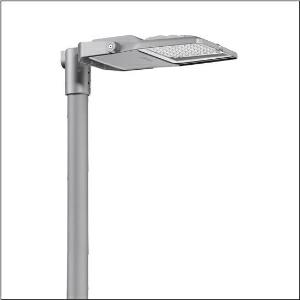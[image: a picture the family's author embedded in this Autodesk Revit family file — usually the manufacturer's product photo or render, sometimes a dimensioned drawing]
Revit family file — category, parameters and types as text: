
# Revit family: floodlight_fl_21_iq_mini___pl52_5xa7772c2d3a_4b1a
name_source: partatom
category: Lighting Fixtures
units: mm (PartAtom-declared; Revit-internal decimal feet)

## family parameters
Cut with Voids When Loaded = No
Host = Face
Light Source = No
Part Type = Normal
Room Calculation Point = No
Round Connector Dimension = Use Diameter
Shared = No

## types (1)
- --- (1 x LED, 12210 lm, 87.2 W, 3000K)
    Apparent Load = 87 VA
    CIE Flux Codes = 26 60 98 100 100
    Color Rendering = 70
    Color Temperature = 3000K
    Default Elevation = 1800 mm
    Description = Floodlight FL 21 iQ mini, floodlight, primary light control with lens, of PMMA, primary optical cover: protective disc, of toughened safety glass, transparent, light distribution: PL52, light emission: direct distribution, installation type: surface-mounted, LED, High Power LED, rated luminous flux: 12.210lm, luminous efficacy: 140lm/W, light colour: 730, colour temperature: 3000K, control: Auto-Match, Temp-Guard, Night-Set, Smart-Wire, Desk-Remote (wireless, voltage-free reading and setting of iQ features in the workshop via application-optimized NFC function/RFID function), optimised constant luminous flux control (CLO 2.0), Light-Fading, Lumen-Switch, with terminal, 6-pole, mains connection: 220..240V, AC, 50/60Hz, start of lifetime: 87W, end of service life: 92W, reduction: 40W, luminaire housing, of diecast aluminium, powder-coated, Siteco® metallic grey (DB 702S), corrosivity category C5 mid according to DIN EN ISO 12944, sealing non-destructively replaceable, please order mast flange separately, mast bracket, of steel, galvanised, powder-coated, protection rating (complete): IP66, insulation class (complete): insulation class II (safety insulation), certification: CE, ENEC, VDE, protection symbol: D, impact resistance: IK08, permissible operating ambient temperature: -40..+40°C, permissible operating ambient temperature for outdoor applications: -40..+50°C, standard: DIN EN 12944, LABS conformity tested according to VDMA 24364:2018-05, packaging unit: 1 piece

Light Distribution: PL52
    Height = 70 mm
    Lamp = 1 x LED
    Lamp Light Flux = 12210 lm
    Lamp Power = 87.2 W
    Lamp count = 1
    Length = 485 mm
    Luminous efficacy = 140 lm/W
    Manufacturer = Siteco
    ModVariant = No
    Model = 5XA7772C2D3A
    Number of Poles = 1
    OnlyDefault = Yes
    Power Factor = 1
    Product Name = Floodlight FL 21 iQ mini | PL52
    Product group = floodlight | pylon annexe
    ProductGroupID = 6200
    Protection Class = Protection class II
    Protection Degree = IP 66
    RLX_Detail_Level = 1
    RLX_Emergency_Light_Flux = 0 lm
    RLX_Emergency_Type = 0
    RLX_Emergency_Type_DB = No
    RlxData = <blob elided: 101513 chars, md5=32d1f423>
    Socket = socket
    Standby Power = 0 W
    System Light Flux = 12210 lm
    System Power = 87 W
    Type Comments = factory setting: luminous flux: 100 % | dim-lin: 254 | 456 mA
    Type Image = l_1007125.jpg
    URL = http://relux.com
    VarID = @adj_114455
    Voltage = 0 V
    Weight = 0.00 kg
    Width = 337 mm

## geometry (parser evidence)
native form markers: Blend x4, Sweep x15
no freeform markers — native parametric forms only
